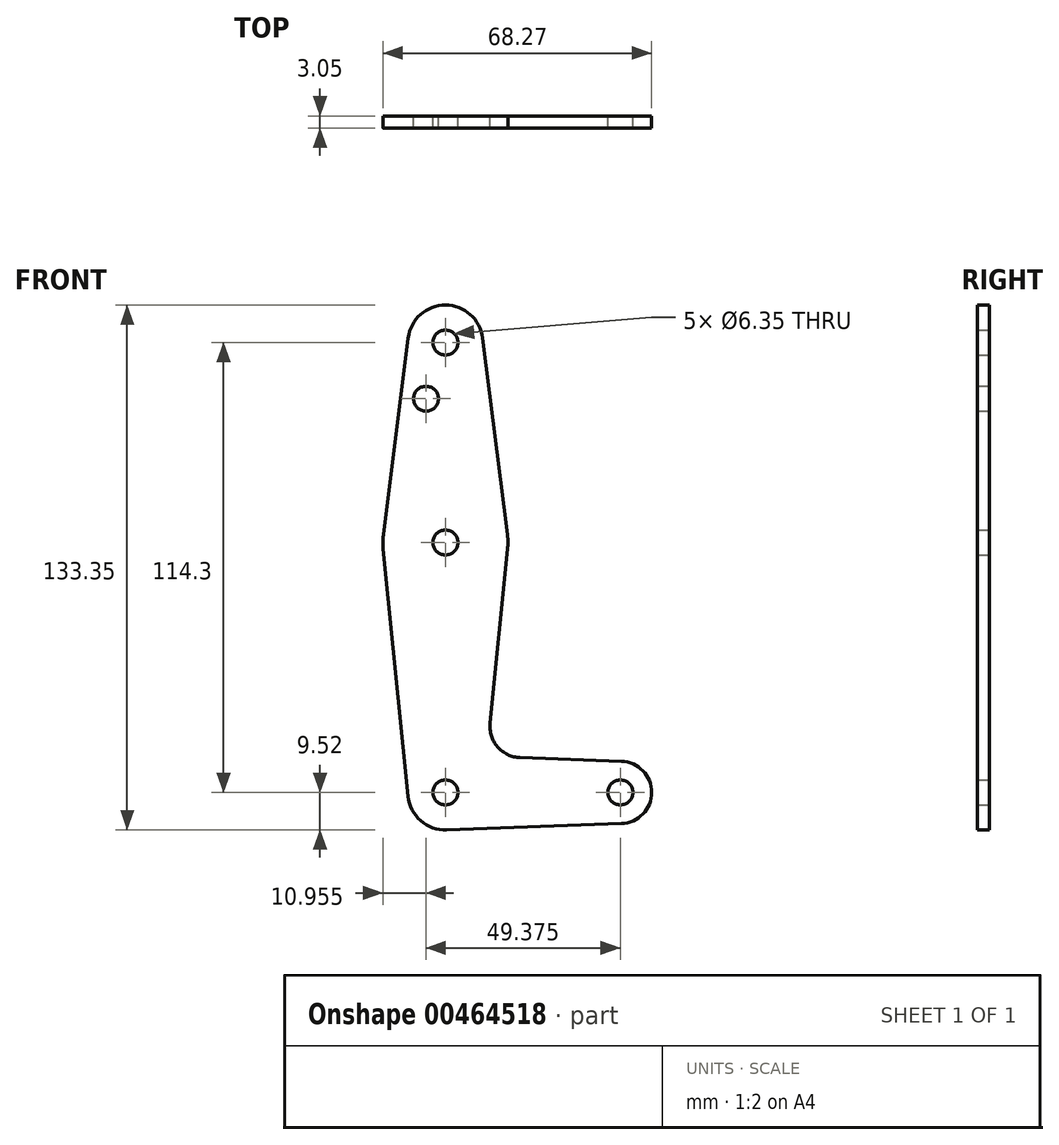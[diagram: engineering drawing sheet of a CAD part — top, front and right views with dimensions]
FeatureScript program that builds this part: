
annotation { "Feature Type Name" : "Feature", "Feature Type Description" : "" }
export const myFeature = defineFeature(function(context is Context, id is Id, definition is map)
    precondition{}
    {
        {
            var Q0;
            Q0=qCreatedBy(makeId("Front.planeOp"),FACE);
            var sketch = newSketch(context, id + "F0", { "sketchPlane" : qUnion([Q0])});
            skLineSegment(sketch, "E0", {"start": v(0, 114.3) * mm, "end": v(0, 0) * mm, "construction": true});
            skLineSegment(sketch, "E1", {"start": v(0, 0) * mm, "end": v(44.45, 0) * mm, "construction": true});
            skCircle(sketch, "E2", {"center": v(0, 114.3) * mm, "radius": 9.53 * mm});
            skCircle(sketch, "E3", {"center": v(0, 0) * mm, "radius": 9.53 * mm});
            skCircle(sketch, "E4", {"center": v(44.45, 0) * mm, "radius": 7.94 * mm});
            skCircle(sketch, "E5", {"center": v(0, 63.5) * mm, "radius": 15.88 * mm});
            skLineSegment(sketch, "E6", {"start": v(9.45, 115.5) * mm, "end": v(15.75, 65.48) * mm});
            skLineSegment(sketch, "E7", {"start": v(-9.45, 115.5) * mm, "end": v(-15.75, 65.48) * mm});
            skLineSegment(sketch, "E8", {"start": v(9.48, -0.95) * mm, "end": v(9.57, 0) * mm});
            skLineSegment(sketch, "E9", {"start": v(-9.48, -0.95) * mm, "end": v(-15.8, 61.91) * mm});
            skLineSegment(sketch, "E10", {"start": v(18.97, 8.85) * mm, "end": v(44.73, 7.93) * mm});
            skLineSegment(sketch, "E11", {"start": v(0.34, -9.52) * mm, "end": v(44.73, -7.93) * mm});
            skCircle(sketch, "E12", {"center": v(0, 114.3) * mm, "radius": 3.18 * mm});
            skCircle(sketch, "E13", {"center": v(0, 63.5) * mm, "radius": 3.18 * mm});
            skCircle(sketch, "E14", {"center": v(0, 0) * mm, "radius": 3.18 * mm});
            skCircle(sketch, "E15", {"center": v(44.45, 0) * mm, "radius": 3.18 * mm});
            skCircle(sketch, "E16", {"center": v(-4.92, 100.03) * mm, "radius": 3.18 * mm});
            skLineSegment(sketch, "E17.trimOffspring", {"start": v(11.34, 17.6) * mm, "end": v(15.8, 61.91) * mm});
            skPoint(sketch, "E18.visualSharp", {"position": v(10.5, 9.16) * mm});
            skArc(sketch, "E18.filletArc", {"start": v(11.34, 17.6) * mm, "mid": v(13.26, 11.57) * mm, "end": v(18.97, 8.85) * mm});
            skSolve(sketch);
        }
        {
            var Q0;
            Q0=makeQuery(id+"F0.imprint","IMPRINT",FACE,{"disambiguationData":[TD([[makeQuery(id+"F0.imprint","IMPRINT",EDGE,{"derivedFrom":sQuery(id+"F0.wireOp",EDGE,"E12")}),-1.0]])]});
            var Q1;
            {var subQ1=sQuery(id+"F0.wireOp",EDGE,"E6");Q1=makeQuery(id+"F0.imprint","IMPRINT",FACE,{"disambiguationData":[TD([[makeQuery(id+"F0.imprint","IMPRINT",EDGE,{"derivedFrom":subQ1}),-1.0]])]});}
            var Q2;
            Q2=makeQuery(id+"F0.imprint","IMPRINT",FACE,{"disambiguationData":[TD([[makeQuery(id+"F0.imprint","IMPRINT",EDGE,{"derivedFrom":sQuery(id+"F0.wireOp",EDGE,"E13")}),-1.0]])]});
            var Q3;
            {var subQ3=sQuery(id+"F0.wireOp",EDGE,"E9");Q3=makeQuery(id+"F0.imprint","IMPRINT",FACE,{"disambiguationData":[TD([[makeQuery(id+"F0.imprint","IMPRINT",EDGE,{"derivedFrom":subQ3}),-1.0]])]});}
            var Q4;
            Q4=makeQuery(id+"F0.imprint","IMPRINT",FACE,{"disambiguationData":[TD([[makeQuery(id+"F0.imprint","IMPRINT",EDGE,{"derivedFrom":sQuery(id+"F0.wireOp",EDGE,"E14")}),-1.0]])]});
            var Q5;
            Q5=makeQuery(id+"F0.imprint","IMPRINT",FACE,{"disambiguationData":[TD([[makeQuery(id+"F0.imprint","IMPRINT",EDGE,{"derivedFrom":sQuery(id+"F0.wireOp",EDGE,"E15")}),-1.0]])]});
            extrude(context, id + "F1", {"entities" : qUnion([Q0, Q1, Q2, Q3, Q4, Q5]), "depth" : 3.05 * mm});
        }
    });
